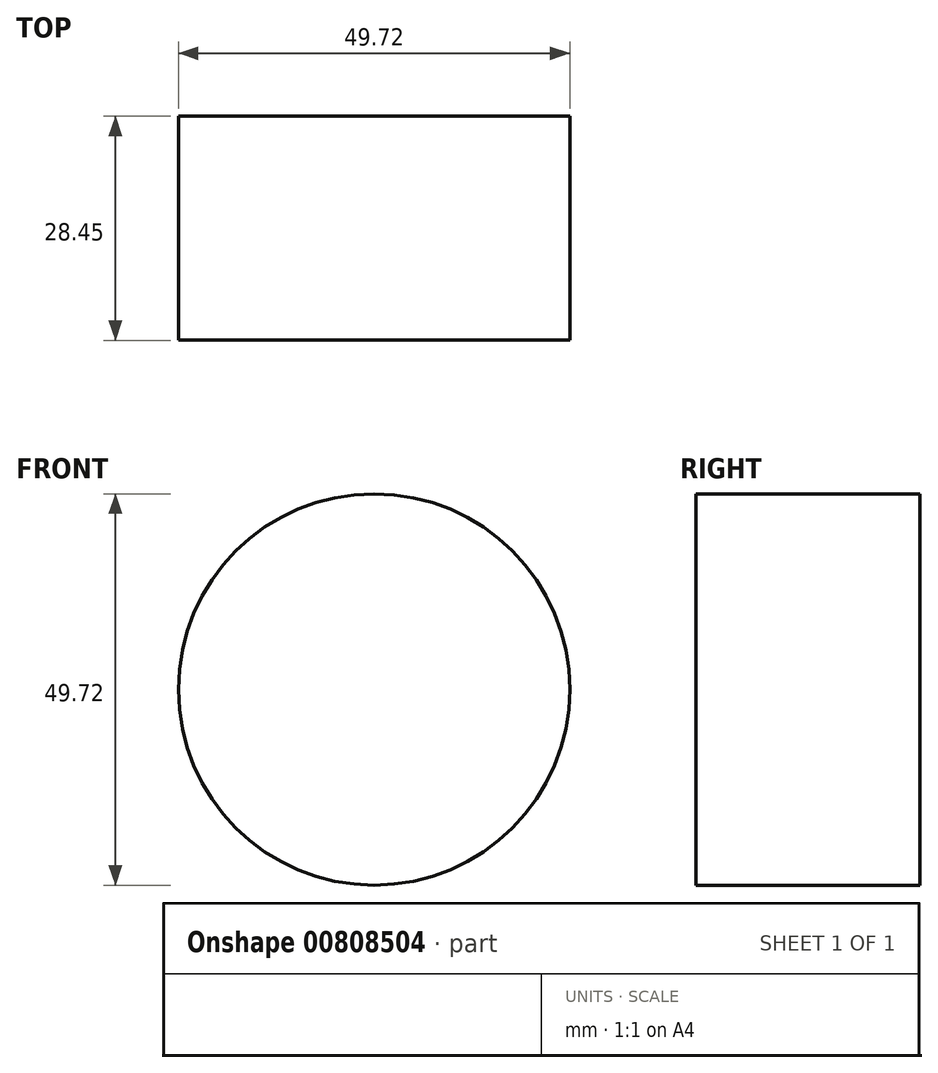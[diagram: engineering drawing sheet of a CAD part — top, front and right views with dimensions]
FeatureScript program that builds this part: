
annotation { "Feature Type Name" : "Feature", "Feature Type Description" : "" }
export const myFeature = defineFeature(function(context is Context, id is Id, definition is map)
    precondition{}
    {
        {
            var Q0;
            Q0=qCreatedBy(makeId("Front.planeOp"),FACE);
            var sketch = newSketch(context, id + "F0", { "sketchPlane" : qUnion([Q0])});
            skCircle(sketch, "E0", {"center": v(25.13, 41.48) * mm, "radius": 24.86 * mm});
            skSolve(sketch);
        }
        {
            var Q0;
            Q0 = qSketchRegion(id + "F0", true);
            extrude(context, id + "F1", {"entities" : qUnion([Q0]), "depth" : 28.45 * mm, "offsetDistance" : 25.4 * mm});
        }
    });
